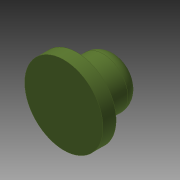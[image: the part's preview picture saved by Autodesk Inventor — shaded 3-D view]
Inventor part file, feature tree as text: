
AUTODESK INVENTOR PART (.ipt)
format: ipt  version: 2014 (Build 180170000, 170)  size: 98,816 bytes
history: native  units: mm
features: extrude x2, sketch x2, other x1, fillet x1
ambient origin geometry x8: Origin, YZ Plane, XZ Plane, XY Plane, X Axis, Y Axis, Z Axis, Center Point
bodies: Body1 (feature_tree)
feature tree (6):
  other  "Твердое тело1"
  extrude  "Выдавливание1"  Depth=6.0mm
  extrude  "Выдавливание2"  Depth=1.0mm TaperAngle=0.0deg
  fillet  "Сопряжение1"  Radius=3.8mm
  sketch  "Эскиз1"
  sketch  "Эскиз2"
